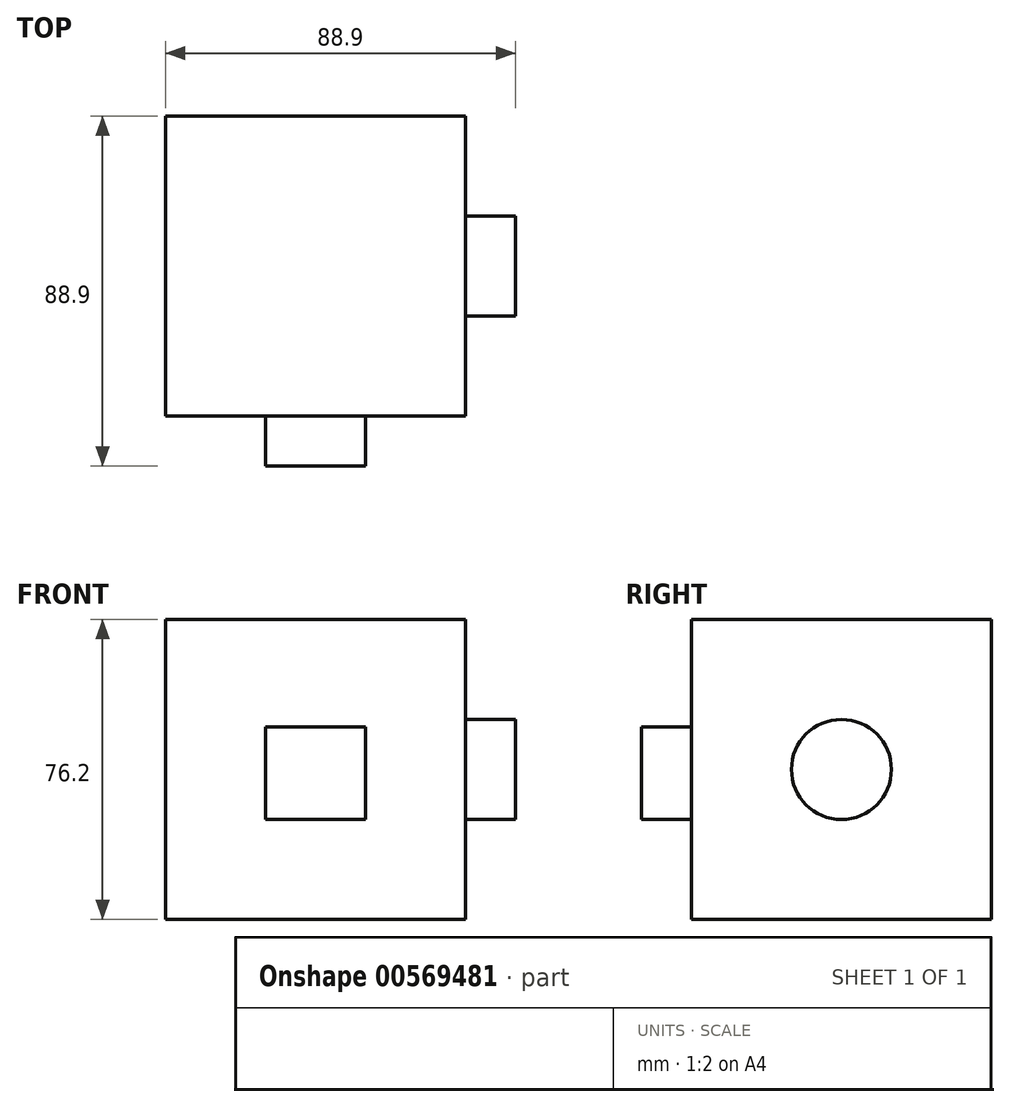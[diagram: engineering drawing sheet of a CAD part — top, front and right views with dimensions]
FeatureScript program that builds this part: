
annotation { "Feature Type Name" : "Feature", "Feature Type Description" : "" }
export const myFeature = defineFeature(function(context is Context, id is Id, definition is map)
    precondition{}
    {
        {
            var Q0;
            Q0=qCreatedBy(makeId("Front.planeOp"),FACE);
            var sketch = newSketch(context, id + "F0", { "sketchPlane" : qUnion([Q0])});
            skLineSegment(sketch, "E0.bottom", {"start": v(-14.23, 73.96) * mm, "end": v(61.97, 73.96) * mm});
            skLineSegment(sketch, "E0.top", {"start": v(-14.23, -2.24) * mm, "end": v(61.97, -2.24) * mm});
            skLineSegment(sketch, "E0.left", {"start": v(-14.23, 73.96) * mm, "end": v(-14.23, -2.24) * mm});
            skLineSegment(sketch, "E0.right", {"start": v(61.97, 73.96) * mm, "end": v(61.97, -2.24) * mm});
            skSolve(sketch);
        }
        {
            var Q0;
            Q0=makeQuery(id+"F0.imprint","IMPRINT",FACE,{"disambiguationData":[TD([[makeQuery(id+"F0.imprint","IMPRINT",EDGE,{"derivedFrom":sQuery(id+"F0.wireOp",EDGE,"E0.bottom")}),-1.0]])]});
            extrude(context, id + "F1", {"entities" : qUnion([Q0]), "depth" : 76.2 * mm, "offsetDistance" : 25.4 * mm});
        }
        {
            var Q0;
            Q0=makeQuery(id+"F1.opExtrude","CAP_FACE",FACE,{"disambiguationData":[OSD([sQuery(id+"F0.wireOp",EDGE,"E0.bottom"),sQuery(id+"F0.wireOp",EDGE,"E0.top"),sQuery(id+"F0.wireOp",EDGE,"E0.left"),sQuery(id+"F0.wireOp",EDGE,"E0.right")])],"isStart":false});
            var sketch = newSketch(context, id + "F2", { "sketchPlane" : qUnion([Q0])});
            skLineSegment(sketch, "E1.bottom", {"start": v(11.17, 46.67) * mm, "end": v(36.57, 46.67) * mm});
            skLineSegment(sketch, "E1.top", {"start": v(11.17, 23.16) * mm, "end": v(36.57, 23.16) * mm});
            skLineSegment(sketch, "E1.left", {"start": v(11.17, 46.67) * mm, "end": v(11.17, 23.16) * mm});
            skLineSegment(sketch, "E1.right", {"start": v(36.57, 46.67) * mm, "end": v(36.57, 23.16) * mm});
            skSolve(sketch);
        }
        {
            var Q0;
            Q0 = qSketchRegion(id + "F2", true);
            extrude(context, id + "F3", {"entities" : qUnion([Q0]), "operationType" : NewBodyOperationType.ADD, "depth" : 12.7 * mm, "offsetDistance" : 25.4 * mm});
        }
        {
            var Q0;
            Q0=makeQuery(id+"F1.opExtrude","SWEPT_FACE",FACE,{"disambiguationData":[OSD([sQuery(id+"F0.wireOp",EDGE,"E0.right")])]});
            var sketch = newSketch(context, id + "F4", { "sketchPlane" : qUnion([Q0])});
            skCircle(sketch, "E2", {"center": v(-38.1, 35.86) * mm, "radius": 12.7 * mm});
            skSolve(sketch);
        }
        {
            var Q0;
            Q0 = qSketchRegion(id + "F4", true);
            extrude(context, id + "F5", {"entities" : qUnion([Q0]), "operationType" : NewBodyOperationType.ADD, "depth" : 12.7 * mm, "offsetDistance" : 25.4 * mm});
        }
    });
